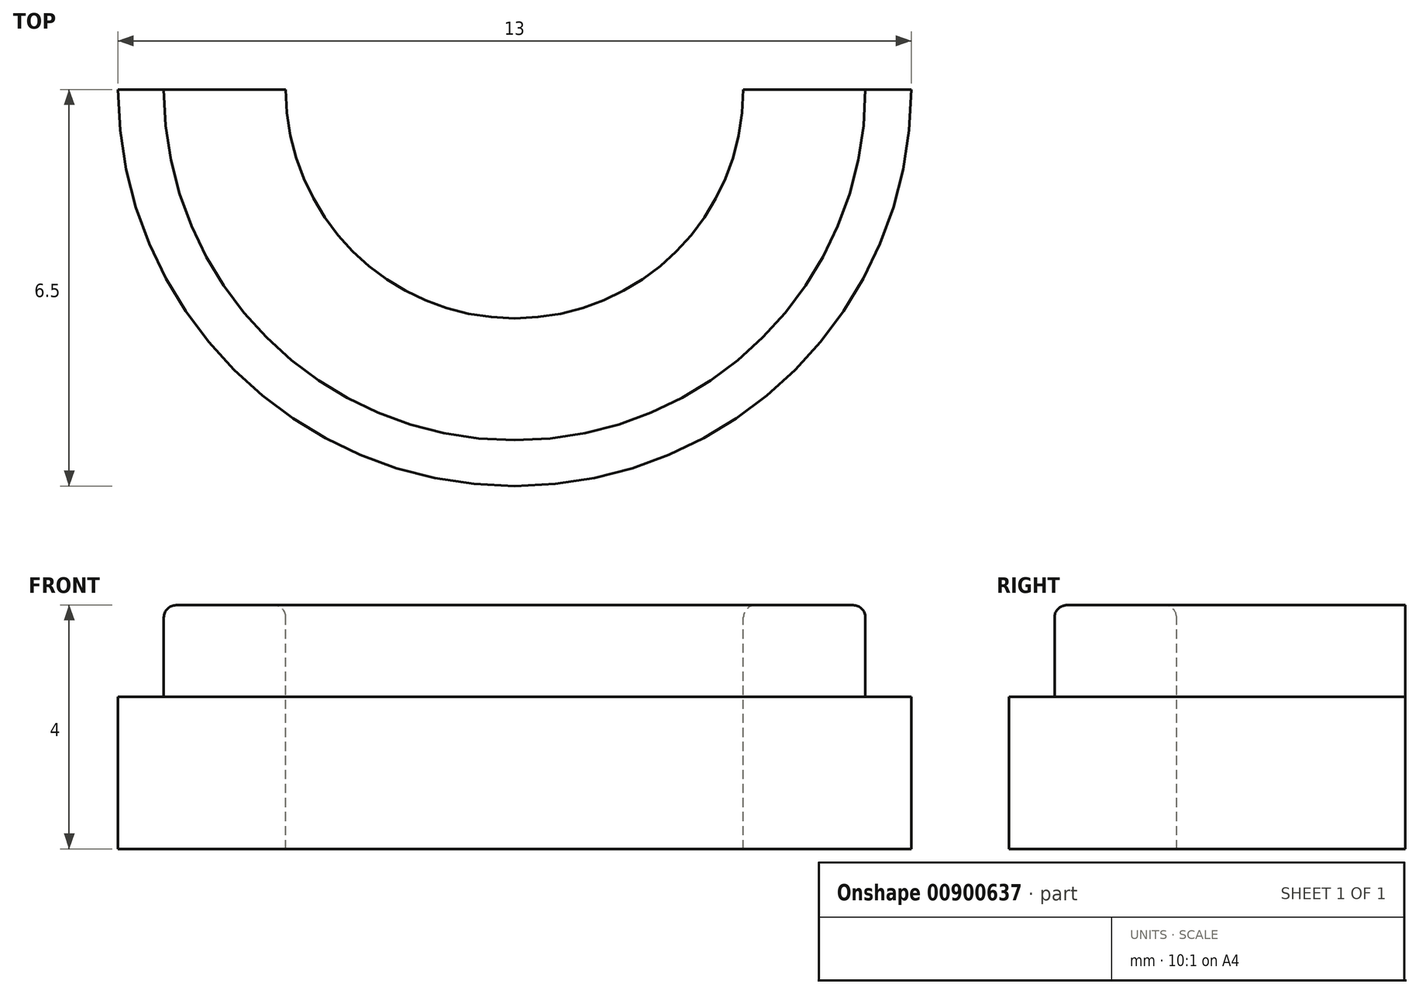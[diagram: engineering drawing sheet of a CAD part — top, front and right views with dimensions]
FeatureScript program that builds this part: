
annotation { "Feature Type Name" : "Feature", "Feature Type Description" : "" }
export const myFeature = defineFeature(function(context is Context, id is Id, definition is map)
    precondition{}
    {
        {
            var Q0;
            Q0=qCreatedBy(makeId("Front.planeOp"),FACE);
            var sketch = newSketch(context, id + "F0", { "sketchPlane" : qUnion([Q0])});
            skLineSegment(sketch, "E0.bottom", {"start": v(20.23, 4.2) * mm, "end": v(22.23, 4.2) * mm});
            skLineSegment(sketch, "E0.top", {"start": v(19.48, 0.2) * mm, "end": v(22.23, 0.2) * mm});
            skLineSegment(sketch, "E0.left", {"start": v(19.48, 2.7) * mm, "end": v(19.48, 0.2) * mm});
            skLineSegment(sketch, "E0.right", {"start": v(22.23, 4.2) * mm, "end": v(22.23, 0.2) * mm});
            skLineSegment(sketch, "E1", {"start": v(20.23, 4.2) * mm, "end": v(20.23, 2.7) * mm});
            skLineSegment(sketch, "E2", {"start": v(20.23, 2.7) * mm, "end": v(19.48, 2.7) * mm});
            skLineSegment(sketch, "E3", {"start": v(25.98, 3.81) * mm, "end": v(25.98, -2.1) * mm, "construction": true});
            skSolve(sketch);
        }
        {
            var Q0;
            Q0=makeQuery(id+"F0.imprint","IMPRINT",FACE,{"disambiguationData":[TD([[makeQuery(id+"F0.imprint","IMPRINT",EDGE,{"derivedFrom":sQuery(id+"F0.wireOp",EDGE,"E0.bottom")}),-1.0]])]});
            var Q1;
            Q1=sQuery(id+"F0.wireOp",EDGE,"E3");
            revolve(context, id + "F1", {"surfaceOperationType" : NewSurfaceOperationType.NEW, "entities" : qUnion([Q0]), "axis" : qUnion([Q1]), "revolveType" : RevolveType.FULL});
        }
        {
            var Q0;
            Q0=qCreatedBy(makeId("Front.planeOp"),FACE);
            var sketch = newSketch(context, id + "F2", { "sketchPlane" : qUnion([Q0])});
            skLineSegment(sketch, "E4.bottom", {"start": v(11.5, 17.53) * mm, "end": v(43.9, 17.53) * mm});
            skLineSegment(sketch, "E4.top", {"start": v(11.5, -14.73) * mm, "end": v(43.9, -14.73) * mm});
            skLineSegment(sketch, "E4.left", {"start": v(11.5, 17.53) * mm, "end": v(11.5, -14.73) * mm});
            skLineSegment(sketch, "E4.right", {"start": v(43.9, 17.53) * mm, "end": v(43.9, -14.73) * mm});
            skSolve(sketch);
        }
        {
            var Q0;
            Q0=makeQuery(id+"F2.imprint","IMPRINT",FACE,{"disambiguationData":[TD([[makeQuery(id+"F2.imprint","IMPRINT",EDGE,{"derivedFrom":sQuery(id+"F2.wireOp",EDGE,"E4.bottom")}),-1.0]])]});
            extrude(context, id + "F3", {"entities" : qUnion([Q0]), "operationType" : NewBodyOperationType.REMOVE, "oppositeDirection" : true, "depth" : 25 * mm, "offsetDistance" : 25 * mm});
        }
        {
            var Q0;
            Q0=makeQuery(id+"F1.opRevolve","SWEPT_EDGE",EDGE,{"disambiguationData":[OSD([sQuery(id+"F0.wireOp",EDGE,"E0.bottom"),sQuery(id+"F0.wireOp",EDGE,"E1")])]});
            var Q1;
            Q1=makeQuery(id+"F1.opRevolve","SWEPT_EDGE",EDGE,{"disambiguationData":[OSD([sQuery(id+"F0.wireOp",EDGE,"E0.bottom"),sQuery(id+"F0.wireOp",EDGE,"E0.right")])]});
            fillet(context, id + "F4", {"entities" : qUnion([Q0, Q1]), "radius" : 0.2 * mm, "tangentPropagation" : true, "allowEdgeOverflow" : false});
        }
    });
